# Revit family: Paramount_Five_115kW
name_source: partatom
category: Mechanical Equipment
units: mm (PartAtom-declared; Revit-internal decimal feet)

## family parameters
Always vertical = Yes
Cut with Voids When Loaded = No
OmniClass Number = 23.75.00.00
OmniClass Title = Climate Control (HVAC)
Part Type = Normal
Room Calculation Point = No
Round Connector Dimension = Use Diameter
Shared = No
Work Plane-Based = No

## types (1)
- Paramount_Five_115kW
    Access Clearance Bottom = 500 mm  [stored 1.64042 ft]
    Access Clearance Front = 600 mm
    Access Clearance Left = 20 mm  [stored 0.0656168 ft]
    Access Clearance Rear = 0 mm  [stored 0 ft]
    Access Clearance Right = 20 mm  [stored 0.0656168 ft]
    Access Clearance Top = 400 mm  [stored 1.31234 ft]
    Air Inlet Connection Size = 160 mm  [stored 0.524934 ft]
    Annually = As per attached URL O & M Manual
    Assembly Code = D3020100
    AssetType = Fixed
    BMS Links = Yes
    Building Regulations Seasonal Efficiency = 95.7
    Burner Control Type = Modulating
    CE Mark = 0085BL0514
    ClassificationName = Uniclass2015
    ClassificationValue = Pr_60_60_08_34
    Colour = BDR White (no RAL number)
    Condensate Centre = 50 mm  [stored 0.164042 ft]
    Condensate Drain Size = 25 mm  [stored 0.082021 ft]
    Condensate Drain Type = Plain
    Condensate Out = 0 mm  [stored 0 ft]
    Configuration = Single boiler
    Control Type = 0 - 10V, Volt free enable, Direct boiler weather compensating control system. Modbus & BACNet available from Potterton
    Default Elevation = 0 mm  [stored 0 ft]
    Drain Connection Size = 0 mm  [stored 0 ft]
    DurationUnit = Years
    Embodied Carbon = 0
    ErP Energy Label = 0
    ErP Rated Efficiency at Full Load = 93.5
    ErP Rated Efficiency at Part Load = 97.8
    ErP Seasonal Efficiency = 0
    Expected Life = 15
    ExpectedLife = 15
    External Material = Steel
    Features = The new generation Paramount Five is a wall hung condensing gas boiler that's meticulously design using the latest tried and tested technology to maximise efficiency. Manufactured to the latest ISO standards, all outputs exceed the requirements of Building Regulations Part L, delivering exceptional energy efficiency and ultra low NOX emissions
    Finish = Powder coated
    Flow and Return Connection Size = 40 mm  [stored 0.131234 ft]
    Flow and Return Connection Type = Threaded
    Flue Connection size = 110 mm  [stored 0.360892 ft]
    Flue or Air Intake Classification = B23,B23P,B33, C13X, C33X,C43X,C53,C53X, C63X,C83,C93X
    Frequency = 50 Hz
    Fuel Connection Size = 25 mm  [stored 0.082021 ft]
    Fuel Connection Type = Threaded
    Full Load Current = 0 A
    Fuse Rating = 5 A
    Gas Consumption rate = 12.2
    Gas Flow = 0 mm  [stored 0 ft]
    Gas, F&R Centre = 80 mm  [stored 0.262467 ft]
    Gross Weight = 84.00 kg
    Heat Exchanger Material = Aluminium
    Heater Operation = Condensing
    Heating Flow = 0 mm  [stored 0 ft]
    Heating Return = 0 mm  [stored 0 ft]
    Hydraulic Resistance at 11C temperature differential = 55900.0
    Hydraulic Resistance at 20C temperature differential = 17800.0
    IK Rating Electrical Enclosure = X4D
    IfcExportAs = IfcBoilerType
    IfcExportType = NOTDEFINED
    InstallationDate = please record on commissioning
    Interlocks = Yes
    Keynote = T32
    Life Cycle Analysis = 0
    Manufacturer = Potterton Commercial
    Manufacturer Website = https://www.pottertoncommercial.co.uk
    ManufacturerName = Potterton
    Maximum Gas Inlet Pressure = 2500.0 Pa
    Maximum Oil Inlet Pressure = 0.0 Pa
    Maximum Operating Pressure = 400000.0 Pa
    Maximum Power Consumption = 200 W
    Minimum Flow Rate at 11C temperature differential = 2.4 L/s
    Minimum Flow Rate at 20C temperature differential = 1.3 L/s
    Minimum Gas Inlet Pressure = 1700.0 Pa
    Minimum Oil Inlet Pressure = 0.0 Pa
    Minimum Operating Pressure = 100000.0 Pa
    Minimum Power Consumption = 0 W
    Mounting = Wall Mounted
    NBSDescription = Gas Fired Condensing Boiler
    NBSReference = 90-40-05/340
    NOx Emissions = 30
    Nominal Gas Inlet Pressure = 1700.0 Pa
    Nominal Oil Inlet Pressure = 0.0 Pa
    NominalDepth = 0 mm  [stored 0 ft]
    NominalHeight = 0 mm  [stored 0 ft]
    NominalLength = 0 mm  [stored 0 ft]
    Oil Consumption rate = 0.0 L/s
    Operation and Maintenance Manual = https://www.pottertoncommercial.co.uk
    Optional Fuel = Gas - LPG
    Overall Height = 852 mm  [stored 2.79528 ft]
    Overall Length = 570 mm  [stored 1.87008 ft]
    Overall Width = 480 mm  [stored 1.5748 ft]
    Primary Fuel = Gas - NG
    Product Literature = https://www.pottertoncommercial.co.uk
    Product Model Number = 7702496
    Product Range = Paramount Five 115kW
    Rated Criteria = 50/30
    Rated Output = 119300 W
    Reference Standard = EU/2016/426 GAR,  92/42/EEC
    Safety Valve Connection Size = 0 mm  [stored 0 ft]
    Shape = Rectangular (Vertical)
    Shipping Weight = 0.00 kg
    Sound Pressure Level = 60 dBA
    Starting Current = 0 A
    Supply Phase = 1
    Turndown Ratio = 4.5:1
    Type = Space heating
    URL = http://www.potterton.co.uk
    Uniclass2015 = Pr_60_60_08
    Voltage = 230 V
    Water Content = 0.01 m³
    Water Treatment Required = Yes
    _BimSpecGuid = 0
    _CurrentRevision = 0
    bottom of cover = 54 mm
    bottom of display 1 = 99 mm
    bottom of display 2 = 91 mm
    control cover top = 248 mm
    cover left = 37 mm
    cover right = 37 mm
    flue centre from back = 152 mm  [stored 0.498688 ft]
    flue centre from side = 163 mm  [stored 0.534777 ft]
    ridge at bottom of cover = 65 mm  [stored 0.213255 ft]
    top of display 1 = 211 mm
    top of display 2 = 198 mm

note: source unit labels omitted for Hydraulic Resistance at 11C temperature differential, Hydraulic Resistance at 20C temperature differential — the stored unit's dimension contradicts the parameter name (converter mislabeling)

note: [stored X ft] marks values corroborated as IEEE doubles in the binary element streams (Revit-internal decimal feet)

## geometry (parser evidence)
native form markers: Sweep x19
no freeform markers — native parametric forms only
